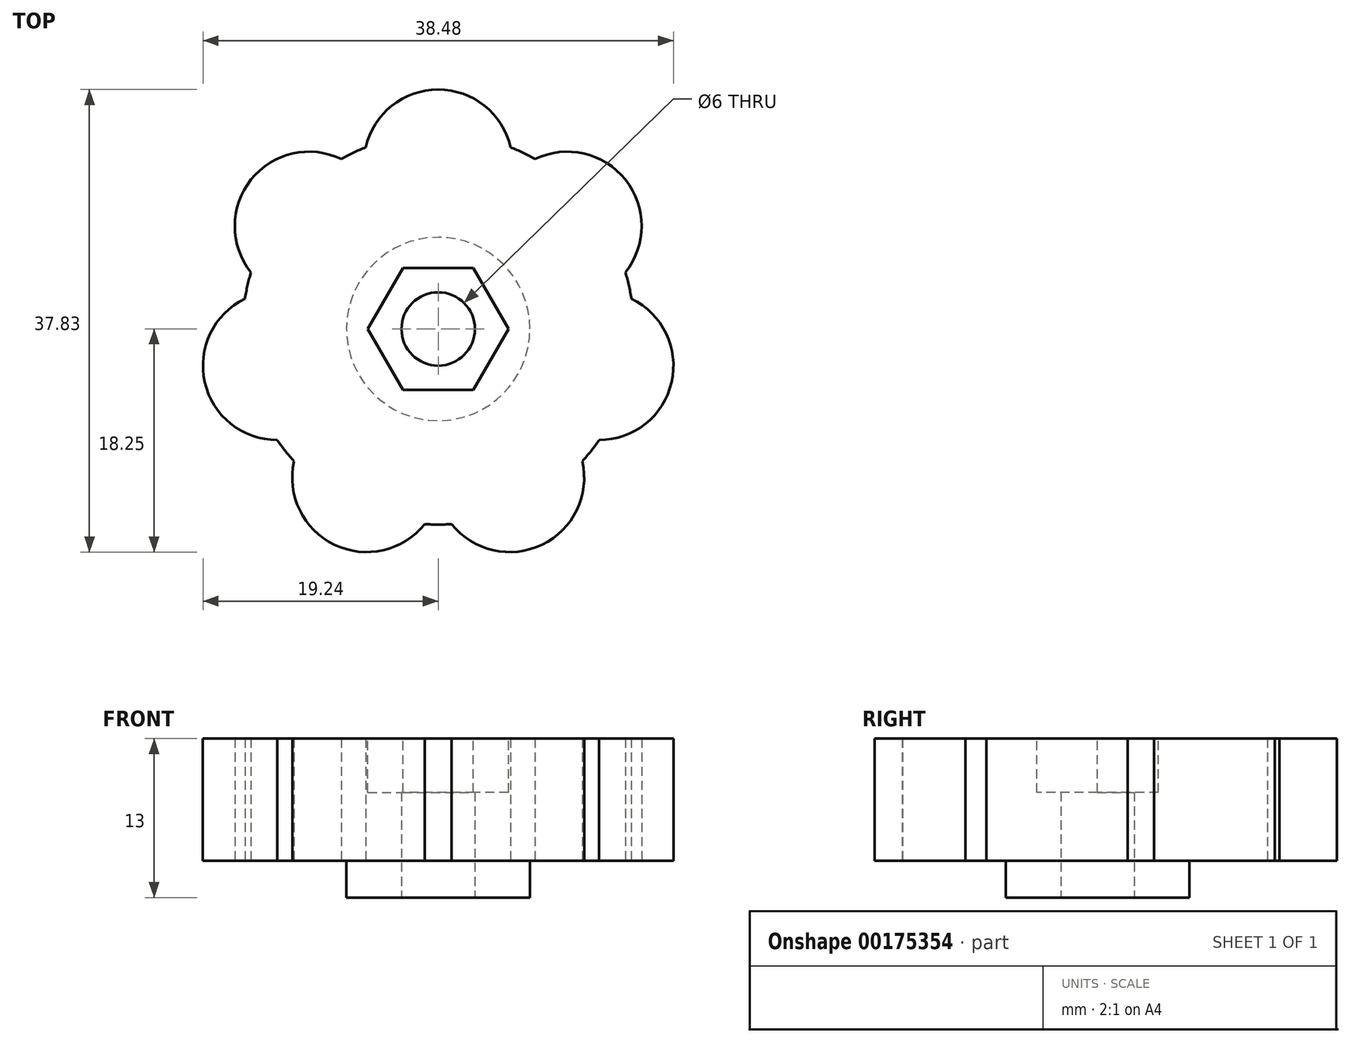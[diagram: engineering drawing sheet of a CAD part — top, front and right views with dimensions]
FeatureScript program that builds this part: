
annotation { "Feature Type Name" : "Feature", "Feature Type Description" : "" }
export const myFeature = defineFeature(function(context is Context, id is Id, definition is map)
    precondition{}
    {
        {
            var Q0;
            Q0=qCreatedBy(makeId("Top.planeOp"),FACE);
            var sketch = newSketch(context, id + "F0", { "sketchPlane" : qUnion([Q0])});
            skArc(sketch, "E0", {"start": v(-5.93, 14.86) * mm, "mid": v(-6.94, 14.42) * mm, "end": v(-7.92, 13.9) * mm});
            skArc(sketch, "E1.2.0", {"start": v(-15.8, 2.47) * mm, "mid": v(-19.1, -4.36) * mm, "end": v(-13.17, -9.09) * mm});
            skArc(sketch, "E1.4.0", {"start": v(1.1, -15.96) * mm, "mid": v(8.5, -17.64) * mm, "end": v(11.79, -10.82) * mm});
            skArc(sketch, "E1.5.0", {"start": v(13.17, -9.09) * mm, "mid": v(19.1, -4.36) * mm, "end": v(15.8, 2.47) * mm});
            skArc(sketch, "E2.trimOffspring", {"start": v(5.93, 14.86) * mm, "mid": v(0, 19.58) * mm, "end": v(-5.93, 14.86) * mm});
            skArc(sketch, "E3.trimOffspring", {"start": v(-15.32, 4.63) * mm, "mid": v(-15.6, 3.56) * mm, "end": v(-15.8, 2.47) * mm});
            skArc(sketch, "E4.trimOffspring", {"start": v(7.92, 13.9) * mm, "mid": v(6.94, 14.42) * mm, "end": v(5.93, 14.86) * mm});
            skArc(sketch, "E5.trimOffspring", {"start": v(15.8, 2.47) * mm, "mid": v(15.6, 3.56) * mm, "end": v(15.32, 4.63) * mm});
            skArc(sketch, "E6.trimOffspring", {"start": v(-7.92, 13.9) * mm, "mid": v(-15.31, 12.2) * mm, "end": v(-15.32, 4.63) * mm});
            skArc(sketch, "E7.trimOffspring", {"start": v(15.32, 4.63) * mm, "mid": v(15.31, 12.2) * mm, "end": v(7.92, 13.9) * mm});
            skArc(sketch, "E8.trimOffspring", {"start": v(11.79, -10.82) * mm, "mid": v(12.5, -9.98) * mm, "end": v(13.17, -9.09) * mm});
            skArc(sketch, "E9.trimOffspring", {"start": v(-1.1, -15.96) * mm, "mid": v(0, -16) * mm, "end": v(1.1, -15.96) * mm});
            skArc(sketch, "E10.trimOffspring", {"start": v(-13.17, -9.09) * mm, "mid": v(-12.5, -9.98) * mm, "end": v(-11.79, -10.82) * mm});
            skArc(sketch, "E11.trimOffspring", {"start": v(-11.79, -10.82) * mm, "mid": v(-8.5, -17.64) * mm, "end": v(-1.1, -15.96) * mm});
            skSolve(sketch);
        }
        {
            var Q0;
            Q0=makeQuery(id+"F0.imprint","IMPRINT",FACE,{"disambiguationData":[TD([[makeQuery(id+"F0.imprint","IMPRINT",EDGE,{"derivedFrom":sQuery(id+"F0.wireOp",EDGE,"E0")}),1.0]])]});
            extrude(context, id + "F1", {"entities" : qUnion([Q0]), "depth" : 10 * mm});
        }
        {
            var Q0;
            Q0=makeQuery(id+"F1.opExtrude","CAP_FACE",FACE,{"disambiguationData":[OSD([sQuery(id+"F0.wireOp",EDGE,"E0"),sQuery(id+"F0.wireOp",EDGE,"E1.2.0"),sQuery(id+"F0.wireOp",EDGE,"E1.4.0"),sQuery(id+"F0.wireOp",EDGE,"E1.5.0"),sQuery(id+"F0.wireOp",EDGE,"E2.trimOffspring"),sQuery(id+"F0.wireOp",EDGE,"E3.trimOffspring"),sQuery(id+"F0.wireOp",EDGE,"E4.trimOffspring"),sQuery(id+"F0.wireOp",EDGE,"E5.trimOffspring"),sQuery(id+"F0.wireOp",EDGE,"E6.trimOffspring"),sQuery(id+"F0.wireOp",EDGE,"E7.trimOffspring"),sQuery(id+"F0.wireOp",EDGE,"E8.trimOffspring"),sQuery(id+"F0.wireOp",EDGE,"E9.trimOffspring"),sQuery(id+"F0.wireOp",EDGE,"E10.trimOffspring"),sQuery(id+"F0.wireOp",EDGE,"E11.trimOffspring")])],"isStart":false});
            var sketch = newSketch(context, id + "F2", { "sketchPlane" : qUnion([Q0])});
            skCircle(sketch, "E12.cCircle", {"center": v(0, 0) * mm, "radius": 5.75 * mm, "construction": true});
            skLineSegment(sketch, "E12.0", {"start": v(5.75, 0) * mm, "end": v(2.88, -4.98) * mm});
            skLineSegment(sketch, "E12.1", {"start": v(2.88, -4.98) * mm, "end": v(-2.87, -4.98) * mm});
            skLineSegment(sketch, "E12.2", {"start": v(-2.87, -4.98) * mm, "end": v(-5.75, 0) * mm});
            skLineSegment(sketch, "E12.3", {"start": v(-5.75, 0) * mm, "end": v(-2.88, 4.98) * mm});
            skLineSegment(sketch, "E12.4", {"start": v(-2.88, 4.98) * mm, "end": v(2.87, 4.98) * mm});
            skLineSegment(sketch, "E12.5", {"start": v(2.87, 4.98) * mm, "end": v(5.75, 0) * mm});
            skSolve(sketch);
        }
        {
            var Q0;
            Q0=makeQuery(id+"F2.imprint","IMPRINT",FACE,{"disambiguationData":[TD([[makeQuery(id+"F2.imprint","IMPRINT",EDGE,{"derivedFrom":sQuery(id+"F2.wireOp",EDGE,"E12.0")}),-1.0]])]});
            extrude(context, id + "F3", {"entities" : qUnion([Q0]), "operationType" : NewBodyOperationType.REMOVE, "oppositeDirection" : true, "depth" : 4.4 * mm});
        }
        {
            var Q0;
            Q0=makeQuery(id+"F1.opExtrude","CAP_FACE",FACE,{"disambiguationData":[OSD([sQuery(id+"F0.wireOp",EDGE,"E0"),sQuery(id+"F0.wireOp",EDGE,"E1.2.0"),sQuery(id+"F0.wireOp",EDGE,"E1.4.0"),sQuery(id+"F0.wireOp",EDGE,"E1.5.0"),sQuery(id+"F0.wireOp",EDGE,"E2.trimOffspring"),sQuery(id+"F0.wireOp",EDGE,"E3.trimOffspring"),sQuery(id+"F0.wireOp",EDGE,"E4.trimOffspring"),sQuery(id+"F0.wireOp",EDGE,"E5.trimOffspring"),sQuery(id+"F0.wireOp",EDGE,"E6.trimOffspring"),sQuery(id+"F0.wireOp",EDGE,"E7.trimOffspring"),sQuery(id+"F0.wireOp",EDGE,"E8.trimOffspring"),sQuery(id+"F0.wireOp",EDGE,"E9.trimOffspring"),sQuery(id+"F0.wireOp",EDGE,"E10.trimOffspring"),sQuery(id+"F0.wireOp",EDGE,"E11.trimOffspring")])],"isStart":true});
            var sketch = newSketch(context, id + "F4", { "sketchPlane" : qUnion([Q0])});
            skCircle(sketch, "E13", {"center": v(0, 0) * mm, "radius": 7.5 * mm});
            skSolve(sketch);
        }
        {
            var Q0;
            Q0=makeQuery(id+"F4.imprint","IMPRINT",FACE,{"disambiguationData":[TD([[makeQuery(id+"F4.imprint","IMPRINT",EDGE,{"derivedFrom":sQuery(id+"F4.wireOp",EDGE,"E13")}),1.0]])]});
            extrude(context, id + "F5", {"entities" : qUnion([Q0]), "operationType" : NewBodyOperationType.ADD, "depth" : 3 * mm});
        }
        {
            var Q0;
            Q0=makeQuery(id+"F5.opExtrude","CAP_FACE",FACE,{"disambiguationData":[OSD([sQuery(id+"F4.wireOp",EDGE,"E13")])],"isStart":false});
            var sketch = newSketch(context, id + "F6", { "sketchPlane" : qUnion([Q0])});
            skCircle(sketch, "E14", {"center": v(0, 0) * mm, "radius": 3 * mm});
            skSolve(sketch);
        }
        {
            var Q0;
            Q0=makeQuery(id+"F6.imprint","IMPRINT",FACE,{"disambiguationData":[TD([[makeQuery(id+"F6.imprint","IMPRINT",EDGE,{"derivedFrom":sQuery(id+"F6.wireOp",EDGE,"E14")}),1.0]])]});
            var Q1;
            Q1=sQuery(id+"F6.wireOp",EDGE,"E14");
            extrude(context, id + "F7", {"entities" : qUnion([Q0]), "operationType" : NewBodyOperationType.REMOVE, "surfaceEntities" : qUnion([Q1]), "endBound" : BoundingType.THROUGH_ALL, "oppositeDirection" : true, "depth" : 25 * mm});
        }
    });
